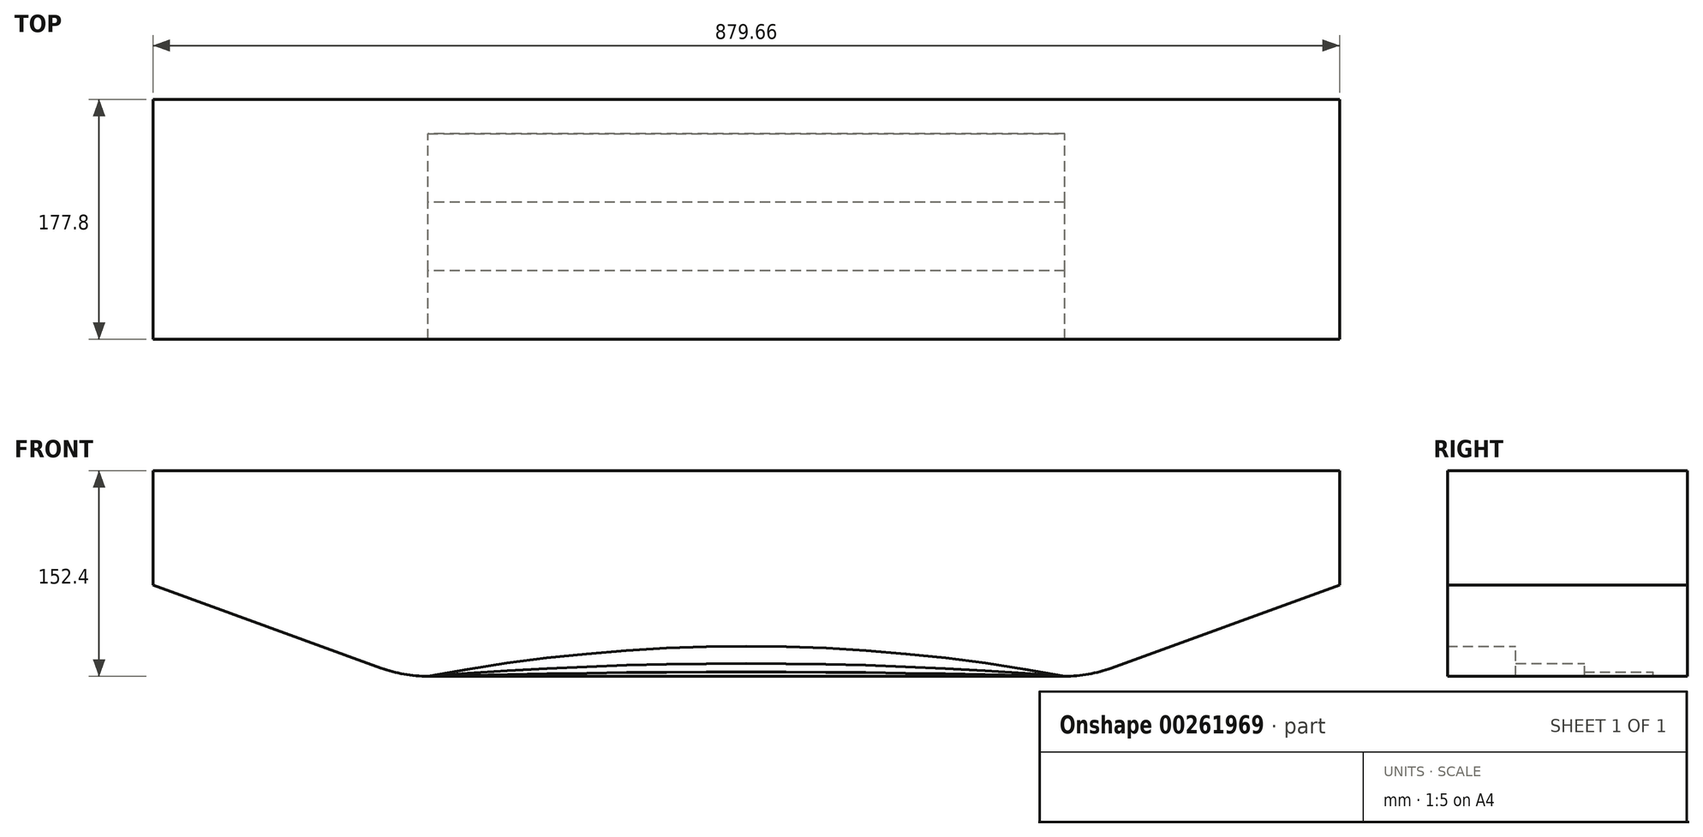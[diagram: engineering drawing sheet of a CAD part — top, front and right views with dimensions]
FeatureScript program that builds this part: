
annotation { "Feature Type Name" : "Feature", "Feature Type Description" : "" }
export const myFeature = defineFeature(function(context is Context, id is Id, definition is map)
    precondition{}
    {
        {
            var Q0;
            Q0=qCreatedBy(makeId("Front.planeOp"),FACE);
            var sketch = newSketch(context, id + "F0", { "sketchPlane" : qUnion([Q0])});
            skLineSegment(sketch, "E0", {"start": v(-254, 11.11) * mm, "end": v(254, 11.11) * mm});
            skLineSegment(sketch, "E1", {"start": v(-254, 11.11) * mm, "end": v(-672.72, 163.51) * mm});
            skLineSegment(sketch, "E2", {"start": v(254, 11.11) * mm, "end": v(672.72, 163.51) * mm});
            skLineSegment(sketch, "E3", {"start": v(-672.72, 163.51) * mm, "end": v(672.72, 163.51) * mm});
            skLineSegment(sketch, "E4", {"start": v(-439.83, 163.51) * mm, "end": v(-439.83, 78.75) * mm});
            skLineSegment(sketch, "E5", {"start": v(439.83, 163.51) * mm, "end": v(439.83, 78.75) * mm});
            skSolve(sketch);
        }
        {
            var Q0;
            {var subQ4=sQuery(id+"F0.wireOp",EDGE,"E0");Q0=makeQuery(id+"F0.imprint","IMPRINT",FACE,{"disambiguationData":[TD([[makeQuery(id+"F0.imprint","IMPRINT",EDGE,{"derivedFrom":subQ4}),1.0]])]});}
            extrude(context, id + "F1", {"entities" : qUnion([Q0]), "depth" : 25.4 * mm});
        }
        {
            var Q0;
            Q0=makeQuery(id+"F1.opExtrude","SWEPT_EDGE",EDGE,{"disambiguationData":[OSD([sQuery(id+"F0.wireOp",EDGE,"E0"),sQuery(id+"F0.wireOp",EDGE,"E1")])]});
            var Q1;
            Q1=makeQuery(id+"F1.opExtrude","SWEPT_EDGE",EDGE,{"disambiguationData":[OSD([sQuery(id+"F0.wireOp",EDGE,"E0"),sQuery(id+"F0.wireOp",EDGE,"E2")])]});
            fillet(context, id + "F2", {"entities" : qUnion([Q0, Q1]), "radius" : 101.6 * mm, "tangentPropagation" : true, "allowEdgeOverflow" : false});
        }
        {
            var Q0;
            Q0=makeQuery(id+"F1.opExtrude","CAP_FACE",FACE,{"disambiguationData":[OSD([sQuery(id+"F0.wireOp",EDGE,"E0"),sQuery(id+"F0.wireOp",EDGE,"E1"),sQuery(id+"F0.wireOp",EDGE,"E2"),sQuery(id+"F0.wireOp",EDGE,"E3"),sQuery(id+"F0.wireOp",EDGE,"E4"),sQuery(id+"F0.wireOp",EDGE,"E5")])],"isStart":false});
            var sketch = newSketch(context, id + "F3", { "sketchPlane" : qUnion([Q0])});
            skArc(sketch, "E6", {"start": v(236.09, 11.11) * mm, "mid": v(0, 14.29) * mm, "end": v(-236.09, 11.11) * mm});
            skLineSegment(sketch, "E7.0", {"start": v(-270.83, 17.24) * mm, "end": v(-439.83, 78.75) * mm});
            skArc(sketch, "E7.1", {"start": v(-270.83, 17.24) * mm, "mid": v(-253.73, 12.66) * mm, "end": v(-236.09, 11.11) * mm});
            skLineSegment(sketch, "E8.0", {"start": v(270.83, 17.24) * mm, "end": v(439.83, 78.75) * mm});
            skArc(sketch, "E8.1", {"start": v(236.09, 11.11) * mm, "mid": v(253.73, 12.66) * mm, "end": v(270.83, 17.24) * mm});
            skLineSegment(sketch, "E9", {"start": v(-439.83, 78.75) * mm, "end": v(-439.83, 163.51) * mm});
            skLineSegment(sketch, "E10", {"start": v(-439.83, 163.51) * mm, "end": v(439.83, 163.51) * mm});
            skLineSegment(sketch, "E11", {"start": v(439.83, 163.51) * mm, "end": v(439.83, 78.75) * mm});
            skSolve(sketch);
        }
        {
            var Q0;
            Q0 = qSketchRegion(id + "F3", true);
            extrude(context, id + "F4", {"entities" : qUnion([Q0]), "operationType" : NewBodyOperationType.ADD, "depth" : 50.8 * mm});
        }
        {
            var Q0;
            Q0=makeQuery(id+"F4.opExtrude","CAP_FACE",FACE,{"disambiguationData":[OSD([sQuery(id+"F3.wireOp",EDGE,"E6"),sQuery(id+"F3.wireOp",EDGE,"E7.0"),sQuery(id+"F3.wireOp",EDGE,"E7.1"),sQuery(id+"F3.wireOp",EDGE,"E8.0"),sQuery(id+"F3.wireOp",EDGE,"E8.1"),sQuery(id+"F3.wireOp",EDGE,"E9"),sQuery(id+"F3.wireOp",EDGE,"E10"),sQuery(id+"F3.wireOp",EDGE,"E11")])],"isStart":false});
            var sketch = newSketch(context, id + "F5", { "sketchPlane" : qUnion([Q0])});
            skArc(sketch, "E12", {"start": v(236.09, 11.11) * mm, "mid": v(0, 20.64) * mm, "end": v(-236.09, 11.11) * mm});
            skLineSegment(sketch, "E13.0", {"start": v(-270.83, 17.24) * mm, "end": v(-439.83, 78.75) * mm});
            skArc(sketch, "E13.1", {"start": v(-270.83, 17.24) * mm, "mid": v(-253.73, 12.66) * mm, "end": v(-236.09, 11.11) * mm});
            skLineSegment(sketch, "E14.0", {"start": v(270.83, 17.24) * mm, "end": v(439.83, 78.75) * mm});
            skArc(sketch, "E14.1", {"start": v(236.09, 11.11) * mm, "mid": v(253.73, 12.66) * mm, "end": v(270.83, 17.24) * mm});
            skLineSegment(sketch, "E15", {"start": v(-439.83, 78.75) * mm, "end": v(-439.83, 163.51) * mm});
            skLineSegment(sketch, "E16", {"start": v(-439.83, 163.51) * mm, "end": v(439.83, 163.51) * mm});
            skLineSegment(sketch, "E17", {"start": v(439.83, 163.51) * mm, "end": v(439.83, 78.75) * mm});
            skSolve(sketch);
        }
        {
            var Q0;
            Q0=makeQuery(id+"F5.imprint","IMPRINT",FACE,{"disambiguationData":[TD([[makeQuery(id+"F5.imprint","IMPRINT",EDGE,{"derivedFrom":sQuery(id+"F5.wireOp",EDGE,"E12")}),-1.0]])]});
            extrude(context, id + "F6", {"entities" : qUnion([Q0]), "operationType" : NewBodyOperationType.ADD, "depth" : 50.8 * mm});
        }
        {
            var Q0;
            Q0=makeQuery(id+"F6.opExtrude","CAP_FACE",FACE,{"disambiguationData":[OSD([sQuery(id+"F5.wireOp",EDGE,"E12"),sQuery(id+"F5.wireOp",EDGE,"E13.0"),sQuery(id+"F5.wireOp",EDGE,"E13.1"),sQuery(id+"F5.wireOp",EDGE,"E14.0"),sQuery(id+"F5.wireOp",EDGE,"E14.1"),sQuery(id+"F5.wireOp",EDGE,"E15"),sQuery(id+"F5.wireOp",EDGE,"E16"),sQuery(id+"F5.wireOp",EDGE,"E17")])],"isStart":false});
            var sketch = newSketch(context, id + "F7", { "sketchPlane" : qUnion([Q0])});
            skArc(sketch, "E18", {"start": v(236.09, 11.11) * mm, "mid": v(0, 33.34) * mm, "end": v(-236.09, 11.11) * mm});
            skArc(sketch, "E19.0", {"start": v(-270.83, 17.24) * mm, "mid": v(-253.73, 12.66) * mm, "end": v(-236.09, 11.11) * mm});
            skLineSegment(sketch, "E19.1", {"start": v(-270.83, 17.24) * mm, "end": v(-439.83, 78.75) * mm});
            skLineSegment(sketch, "E20.0", {"start": v(270.83, 17.24) * mm, "end": v(439.83, 78.75) * mm});
            skArc(sketch, "E20.1", {"start": v(236.09, 11.11) * mm, "mid": v(253.73, 12.66) * mm, "end": v(270.83, 17.24) * mm});
            skLineSegment(sketch, "E21", {"start": v(-439.83, 78.75) * mm, "end": v(-439.83, 163.51) * mm});
            skLineSegment(sketch, "E22", {"start": v(-439.83, 163.51) * mm, "end": v(439.83, 163.51) * mm});
            skLineSegment(sketch, "E23", {"start": v(439.83, 163.51) * mm, "end": v(439.83, 78.75) * mm});
            skSolve(sketch);
        }
        {
            var Q0;
            Q0=makeQuery(id+"F7.imprint","IMPRINT",FACE,{"disambiguationData":[TD([[makeQuery(id+"F7.imprint","IMPRINT",EDGE,{"derivedFrom":sQuery(id+"F7.wireOp",EDGE,"E18")}),-1.0]])]});
            extrude(context, id + "F8", {"entities" : qUnion([Q0]), "operationType" : NewBodyOperationType.ADD, "depth" : 50.8 * mm});
        }
    });
